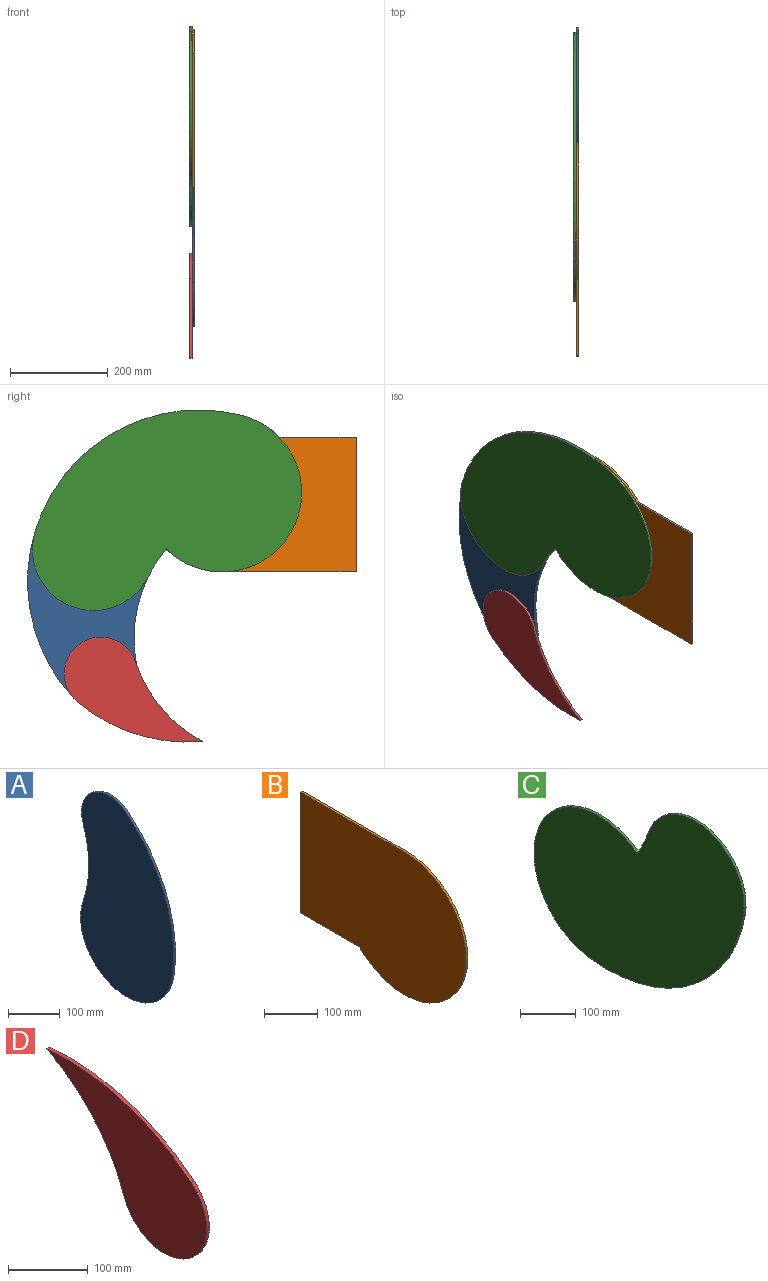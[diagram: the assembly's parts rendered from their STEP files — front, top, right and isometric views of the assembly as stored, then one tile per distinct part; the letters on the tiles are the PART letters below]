
ASSEMBLY  parts=4 mates=3
PART A: 6 faces, bbox 5x253.1x450 mm
  f0: cylinder r=125mm len=248.27mm, axis (1,0,0), area 2065.6mm2, adj f1,f3,f4,f5
  f1: cylinder r=284.64mm len=185.04mm, axis (1,0,0), area 942.3mm2, adj f0,f2,f4,f5
  f2: cylinder r=75mm len=122.55mm, axis (1,0,0), area 971.1mm2, adj f1,f3,f4,f5
  f3: cylinder r=350mm len=328.74mm, axis (1,0,0), area 1838.9mm2, adj f0,f2,f4,f5
  f4: plane 450x253.12mm, normal (-1,0,0), area 89079.8mm2, adj f0,f1,f2,f3
  f5: plane 450x253.12mm, normal (1,0,0), area 89079.8mm2, adj f0,f1,f2,f3
PART B: 6 faces, bbox 5x436.1x325 mm
  f0: cylinder r=162.5mm len=325mm, axis (1,0,0), area 3207.5mm2, adj f1,f3,f4,f5
  f1: plane 156.39x5mm, normal (0,0,-1), area 781.9mm2, adj f0,f2,f4,f5
  f2: plane 275x5mm, normal (0,1,0), area 1375mm2, adj f1,f3,f4,f5
  f3: plane 273.65x5mm, normal (0,0,1), area 1368.2mm2, adj f0,f2,f4,f5
  f4: plane 436.15x325mm, normal (-1,0,0), area 120779.8mm2, adj f0,f1,f2,f3
  f5: plane 436.15x325mm, normal (1,0,0), area 120779.8mm2, adj f0,f1,f2,f3
PART C: 6 faces, bbox 5x533.6x437.7 mm
  f0: cylinder r=350mm len=390.39mm, axis (-1,0,0), area 2684.1mm2, adj f1,f3,f4,f5
  f1: cylinder r=162.5mm len=323.64mm, axis (-1,0,0), area 2979.2mm2, adj f0,f2,f4,f5
  f2: cylinder r=284.64mm len=60.21mm, axis (-1,0,0), area 334.7mm2, adj f1,f3,f4,f5
  f3: cylinder r=125mm len=243.25mm, axis (-1,0,0), area 1861.4mm2, adj f0,f2,f4,f5
  f4: plane 533.62x437.68mm, normal (1,0,0), area 157110.1mm2, adj f0,f1,f2,f3
  f5: plane 533.62x437.68mm, normal (-1,0,0), area 157110.1mm2, adj f0,f1,f2,f3
PART D: 5 faces, bbox 5x284.2x212.3 mm
  f0: cylinder r=284.64mm len=160.03mm, axis (-1,0,0), area 1083.7mm2, adj f1,f2,f3,f4
  f1: cylinder r=350mm len=256.79mm, axis (-1,0,0), area 1376.5mm2, adj f0,f2,f3,f4
  f2: cylinder r=75mm len=145.9mm, axis (-1,0,0), area 1385.1mm2, adj f0,f1,f3,f4
  f3: plane 284.24x212.32mm, normal (1,0,0), area 28964.9mm2, adj f0,f1,f2
  f4: plane 284.24x212.32mm, normal (-1,0,0), area 28964.9mm2, adj f0,f1,f2
PLACE A rot(axis=(-1,0,0),172.6deg) t=(0,464.41,-196.58)mm
PLACE B rot(axis=(-1,0,0),180deg) t=(0,447.61,-228.85)mm fixed
PLACE C rot(axis=(-1,0,0),172.7deg) t=(-10,464.41,-196.58)mm
PLACE D rot(axis=(-1,0,0),179.2deg) t=(-10,493.56,-199.99)mm
MATE revolute C.f3 <-> A.f0  axis (1,0,0) through (-5,464.41,-196.58)mm
MATE revolute D.f2 <-> A.f2  axis (1,0,0) through (-5,449.41,-450.61)mm
MATE revolute C.f1 <-> B.f0  axis (1,0,0) through (-5,201.5,-80.24)mm
